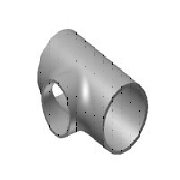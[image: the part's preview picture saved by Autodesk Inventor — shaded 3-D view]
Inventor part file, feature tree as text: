
AUTODESK INVENTOR PART (.ipt)
format: ipt  version: 2023.2 (Build 272271030, 271C)  size: 240,128 bytes
history: native  units: mm
features: other x6, extrude x4, sketch x4, fillet x2
ambient origin geometry x8: Origin, YZ Plane, XZ Plane, XY Plane, X Axis, Y Axis, Z Axis, Center Point
bodies: Solid1 (feature_tree)
feature tree (16):
  extrude  "Extrusion1"  Depth=200.0mm
  extrude  "Extrusion2"  Depth=76.0mm
  fillet  "Fillet1"  Radius=80.0mm
  extrude  "Extrusion3"  Depth=20.0mm
  extrude  "Extrusion4"  Depth=80.0mm
  fillet  "Fillet2"  [1 undecoded]
  other  "Work Point1"
  other  "Work Point2"
  other  "Work Point3"
  other  "Work Axis1"
  other  "Work Axis2"
  other  "Work Axis3"
  sketch  "Sketch1"  dims[d0=108.0mm d2=200.0mm]
  sketch  "Sketch2"  dims[d3=0.0mm d4=76.0mm d6=80.0mm]
  sketch  "Sketch3"  dims[d7=0.0mm d8=20.0mm]
  sketch  "Sketch4"  dims[d9=69.0mm d10=80.0mm d11=0.0mm d12=100.0mm d13=80.0mm d14=0.0mm d15=24.0mm]
note: 1 required parameter value undecoded (feature->parameter linkage not recoverable at this tier; creation-order binding heuristic only, values carry confidence <= 0.55)
